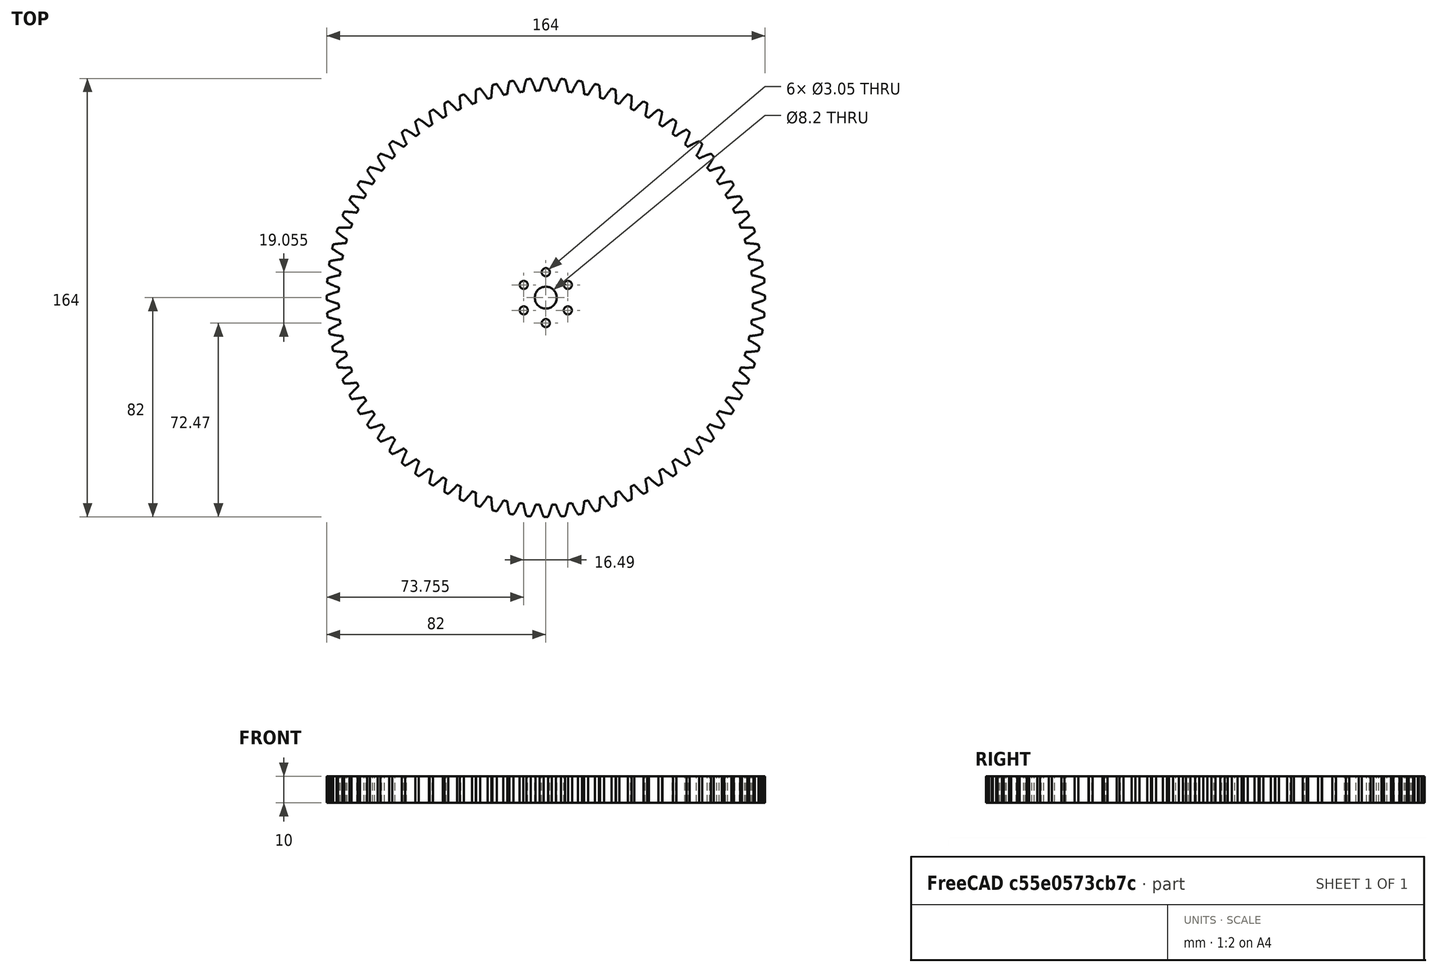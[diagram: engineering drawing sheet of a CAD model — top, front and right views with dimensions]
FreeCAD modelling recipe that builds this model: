
FCSTD DOCUMENT  (FreeCAD 0.19R17798 (Git))
Label: gear80
License: All rights reserved
LicenseURL: http://en.wikipedia.org/wiki/All_rights_reserved
objects: Part::Cylinder×7, Part::Cut×7, Part::FeaturePython×1
note: 15 computed .brp shape members not serialized (recipe doc carries the construction recipe); baked Part::Feature solids carry a one-line shape summary decoded from their .brp

FEATURE [Part::FeaturePython] InvoluteGear  # WARN: FeaturePython — macro-defined, semantics opaque (R4)
  backlash = 0
  beta = 0
  clearance = 0.25
  double_helix = false
  head = 0
  height = 10
  module = 2
  numpoints = 6
  pressure_angle = 20
  reversed_backlash = false
  shift = 0
  simple = false
  teeth = 80
  undercut = false
FEATURE [Part::Cylinder] Cylinder
  Angle = 360
  AttacherType = Attacher::AttachEngine3D
  Height = 30
  Placement = pos=(0,0,-10) rot=(0,0,1;0rad)
  Radius = 4.1
FEATURE [Part::Cylinder] Cylinder001
  Angle = 360
  AttacherType = Attacher::AttachEngine3D
  Height = 30
  Placement = pos=(8.245,4.762,-10) rot=(0,0,1;0rad)
  Radius = 1.525
FEATURE [Part::Cylinder] Cylinder002
  Angle = 360
  AttacherType = Attacher::AttachEngine3D
  Height = 30
  Placement = pos=(0,9.525,-10) rot=(0,0,1;0rad)
  Radius = 1.525
FEATURE [Part::Cylinder] Cylinder003
  Angle = 360
  AttacherType = Attacher::AttachEngine3D
  Height = 30
  Placement = pos=(-8.245,4.762,-10) rot=(0,0,1;0rad)
  Radius = 1.525
FEATURE [Part::Cylinder] Cylinder004
  Angle = 360
  AttacherType = Attacher::AttachEngine3D
  Height = 30
  Placement = pos=(-8.245,-4.762,-10) rot=(0,0,1;0rad)
  Radius = 1.525
FEATURE [Part::Cylinder] Cylinder005
  Angle = 360
  AttacherType = Attacher::AttachEngine3D
  Height = 30
  Placement = pos=(0,-9.53,-10) rot=(0,0,1;0rad)
  Radius = 1.525
FEATURE [Part::Cylinder] Cylinder006
  Angle = 360
  AttacherType = Attacher::AttachEngine3D
  Height = 30
  Placement = pos=(8.245,-4.76,-10) rot=(0,0,1;0rad)
  Radius = 1.525
FEATURE [Part::Cut] Cut
  Base = -> InvoluteGear
  Refine = true
  Tool = -> Cylinder
FEATURE [Part::Cut] Cut001
  Base = -> Cut
  Refine = true
  Tool = -> Cylinder001
FEATURE [Part::Cut] Cut002
  Base = -> Cut001
  Refine = true
  Tool = -> Cylinder002
FEATURE [Part::Cut] Cut003
  Base = -> Cut002
  Refine = true
  Tool = -> Cylinder003
FEATURE [Part::Cut] Cut004
  Base = -> Cut003
  Refine = true
  Tool = -> Cylinder004
FEATURE [Part::Cut] Cut005
  Base = -> Cut004
  Refine = true
  Tool = -> Cylinder005
FEATURE [Part::Cut] Cut006
  Base = -> Cut005
  Refine = true
  Tool = -> Cylinder006
